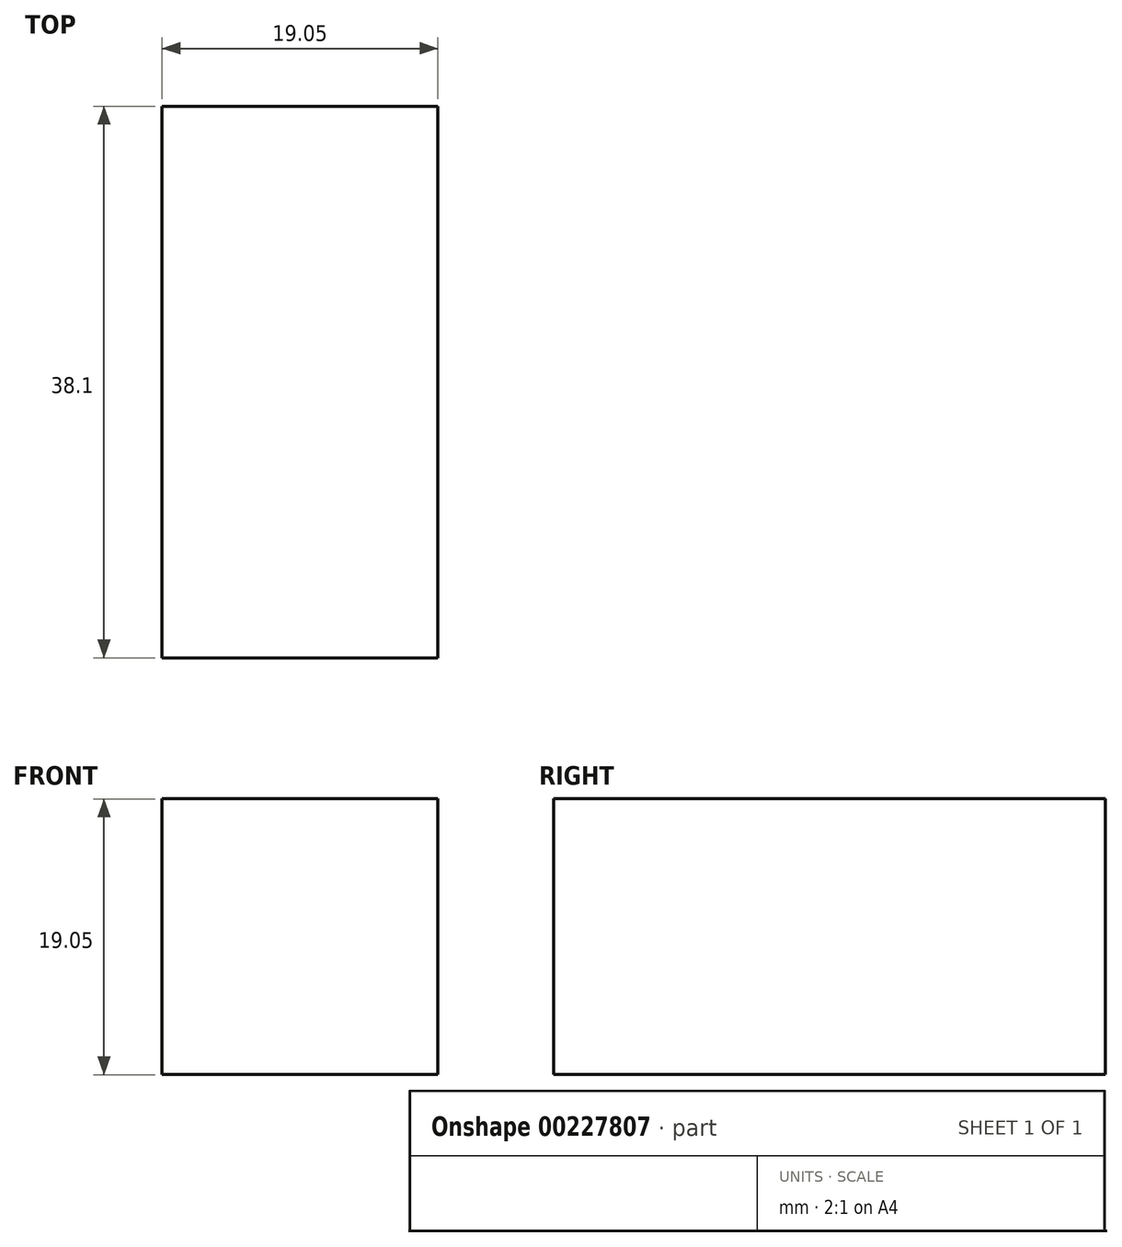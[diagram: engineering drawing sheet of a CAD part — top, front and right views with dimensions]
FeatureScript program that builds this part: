
annotation { "Feature Type Name" : "Feature", "Feature Type Description" : "" }
export const myFeature = defineFeature(function(context is Context, id is Id, definition is map)
    precondition{}
    {
        {
            var Q0;
            Q0=qCreatedBy(makeId("Front.planeOp"),FACE);
            var sketch = newSketch(context, id + "F0", { "sketchPlane" : qUnion([Q0])});
            skLineSegment(sketch, "E0.bottom", {"start": v(-29.54, 29.25) * mm, "end": v(-10.49, 29.25) * mm});
            skLineSegment(sketch, "E0.top", {"start": v(-29.54, 10.2) * mm, "end": v(-10.49, 10.2) * mm});
            skLineSegment(sketch, "E0.left", {"start": v(-29.54, 29.25) * mm, "end": v(-29.54, 10.2) * mm});
            skLineSegment(sketch, "E0.right", {"start": v(-10.49, 29.25) * mm, "end": v(-10.49, 10.2) * mm});
            skSolve(sketch);
        }
        {
            var Q0;
            Q0 = qSketchRegion(id + "F0", true);
            extrude(context, id + "F1", {"entities" : qUnion([Q0]), "oppositeDirection" : true, "depth" : 38.1 * mm});
        }
    });
